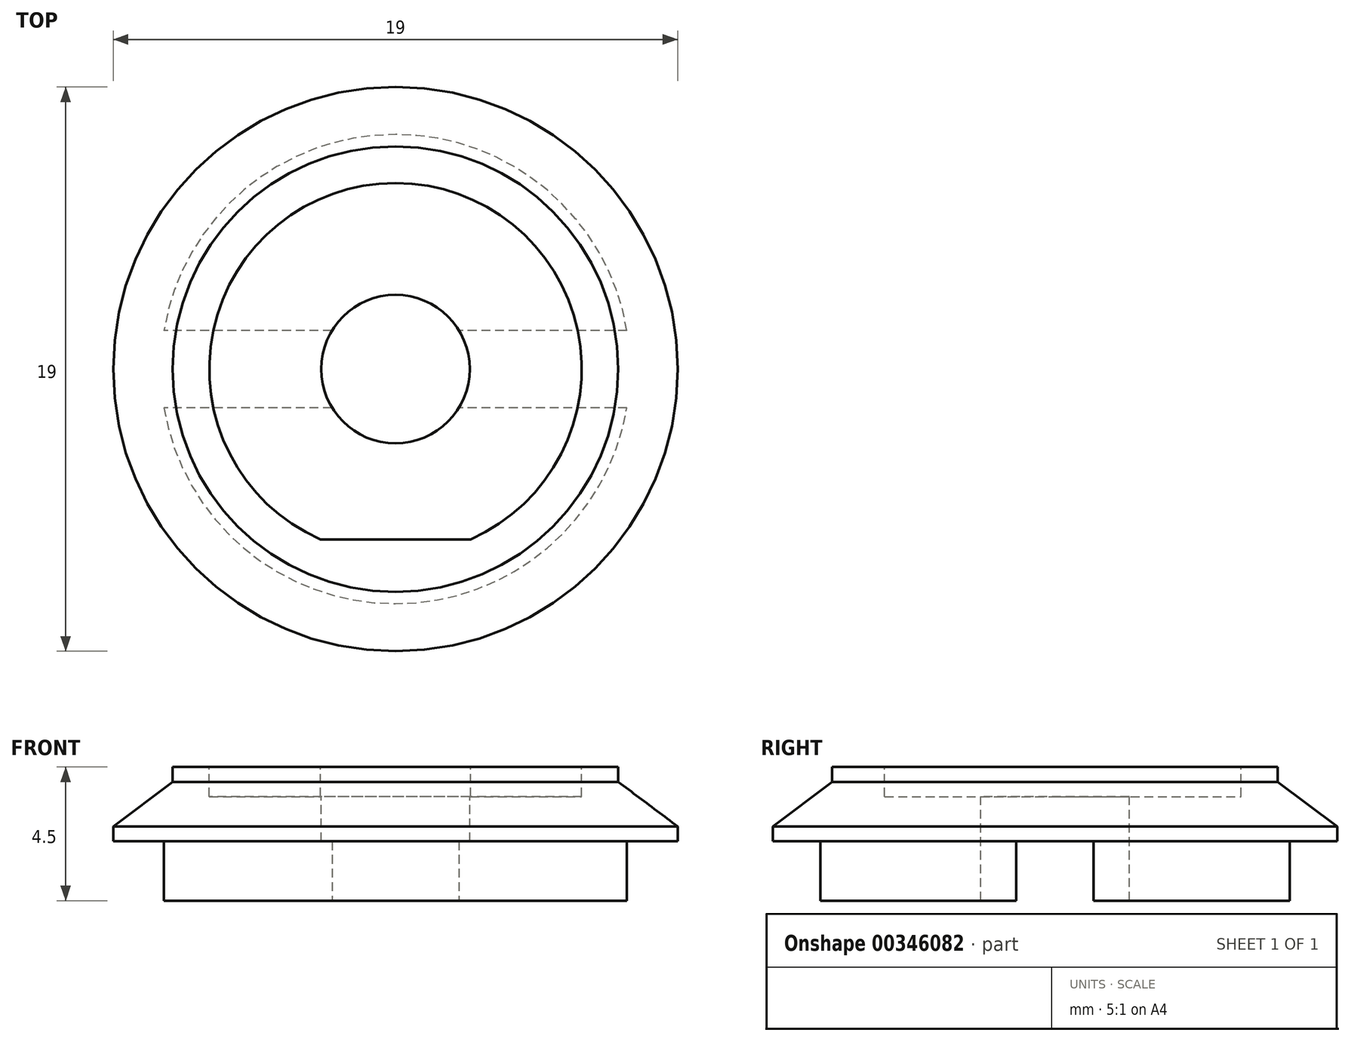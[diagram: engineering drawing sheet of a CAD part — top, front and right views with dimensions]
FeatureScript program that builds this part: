
annotation { "Feature Type Name" : "Feature", "Feature Type Description" : "" }
export const myFeature = defineFeature(function(context is Context, id is Id, definition is map)
    precondition{}
    {
        {
            var Q0;
            Q0=qCreatedBy(makeId("Front.planeOp"),FACE);
            var sketch = newSketch(context, id + "F0", { "sketchPlane" : qUnion([Q0])});
            skLineSegment(sketch, "E0", {"start": v(2.5, 0.69) * mm, "end": v(9.5, 0.69) * mm});
            skLineSegment(sketch, "E1", {"start": v(9.5, 0.69) * mm, "end": v(9.5, 1.19) * mm});
            skLineSegment(sketch, "E2", {"start": v(9.5, 1.19) * mm, "end": v(7.5, 2.69) * mm});
            skLineSegment(sketch, "E3", {"start": v(7.5, 2.69) * mm, "end": v(7.5, 3.19) * mm});
            skLineSegment(sketch, "E4", {"start": v(7.5, 3.19) * mm, "end": v(2.5, 3.19) * mm});
            skLineSegment(sketch, "E5", {"start": v(2.5, 3.19) * mm, "end": v(2.5, 0.69) * mm});
            skLineSegment(sketch, "E6", {"start": v(2.5, 3.19) * mm, "end": v(0, 3.19) * mm});
            skLineSegment(sketch, "E7", {"start": v(0, 3.19) * mm, "end": v(0, 0.69) * mm});
            skLineSegment(sketch, "E8", {"start": v(0, 0.69) * mm, "end": v(2.5, 0.69) * mm});
            skSolve(sketch);
        }
        {
            var Q0;
            Q0=makeQuery(id+"F0.imprint","IMPRINT",FACE,{"disambiguationData":[TD([[makeQuery(id+"F0.imprint","IMPRINT",EDGE,{"derivedFrom":sQuery(id+"F0.wireOp",EDGE,"E0")}),1.0]])]});
            var Q1;
            Q1=sQuery(id+"F0.wireOp",EDGE,"E7");
            revolve(context, id + "F1", {"entities" : qUnion([Q0]), "axis" : qUnion([Q1]), "revolveType" : RevolveType.FULL});
        }
        {
            var Q0;
            Q0=makeQuery(id+"F1.opRevolve","SWEPT_FACE",FACE,{"disambiguationData":[OSD([sQuery(id+"F0.wireOp",EDGE,"E0")])]});
            var sketch = newSketch(context, id + "F2", { "sketchPlane" : qUnion([Q0])});
            skCircle(sketch, "E9", {"center": v(0, 0) * mm, "radius": 7.9 * mm});
            skSolve(sketch);
        }
        {
            var Q0;
            Q0 = qSketchRegion(id + "F2", true);
            extrude(context, id + "F3", {"entities" : qUnion([Q0]), "operationType" : NewBodyOperationType.ADD, "depth" : 2 * mm});
        }
        {
            var Q0;
            Q0=makeQuery(id+"F3.opExtrude","CAP_FACE",FACE,{"disambiguationData":[OSD([sQuery(id+"F2.wireOp",EDGE,"E9")])],"isStart":false});
            var sketch = newSketch(context, id + "F4", { "sketchPlane" : qUnion([Q0])});
            skCircle(sketch, "E10", {"center": v(0, 0) * mm, "radius": 2.5 * mm});
            skLineSegment(sketch, "E11.bottom", {"start": v(8.27, -1.3) * mm, "end": v(-8.27, -1.3) * mm});
            skLineSegment(sketch, "E11.top", {"start": v(8.27, 1.3) * mm, "end": v(-8.27, 1.3) * mm});
            skLineSegment(sketch, "E11.left", {"start": v(8.27, -1.3) * mm, "end": v(8.27, 1.3) * mm});
            skLineSegment(sketch, "E11.right", {"start": v(-8.27, -1.3) * mm, "end": v(-8.27, 1.3) * mm});
            skSolve(sketch);
        }
        {
            var Q0;
            Q0 = qSketchRegion(id + "F4", true);
            extrude(context, id + "F5", {"entities" : qUnion([Q0]), "operationType" : NewBodyOperationType.REMOVE, "oppositeDirection" : true, "depth" : 2 * mm});
        }
        {
            var Q0;
            Q0=makeQuery(id+"F1.opRevolve","SWEPT_FACE",FACE,{"disambiguationData":[OSD([sQuery(id+"F0.wireOp",EDGE,"E4")])]});
            var sketch = newSketch(context, id + "F6", { "sketchPlane" : qUnion([Q0])});
            skArc(sketch, "E12", {"start": v(2.53, -5.73) * mm, "mid": v(0, 6.27) * mm, "end": v(-2.53, -5.73) * mm});
            skLineSegment(sketch, "E13", {"start": v(2.53, -5.73) * mm, "end": v(0, -5.73) * mm});
            skLineSegment(sketch, "E14.MirrorCS", {"start": v(-2.53, -5.73) * mm, "end": v(0, -5.73) * mm});
            skSolve(sketch);
        }
        {
            var Q0;
            Q0 = qSketchRegion(id + "F6", true);
            extrude(context, id + "F7", {"entities" : qUnion([Q0]), "operationType" : NewBodyOperationType.REMOVE, "oppositeDirection" : true, "depth" : 1 * mm});
        }
    });
